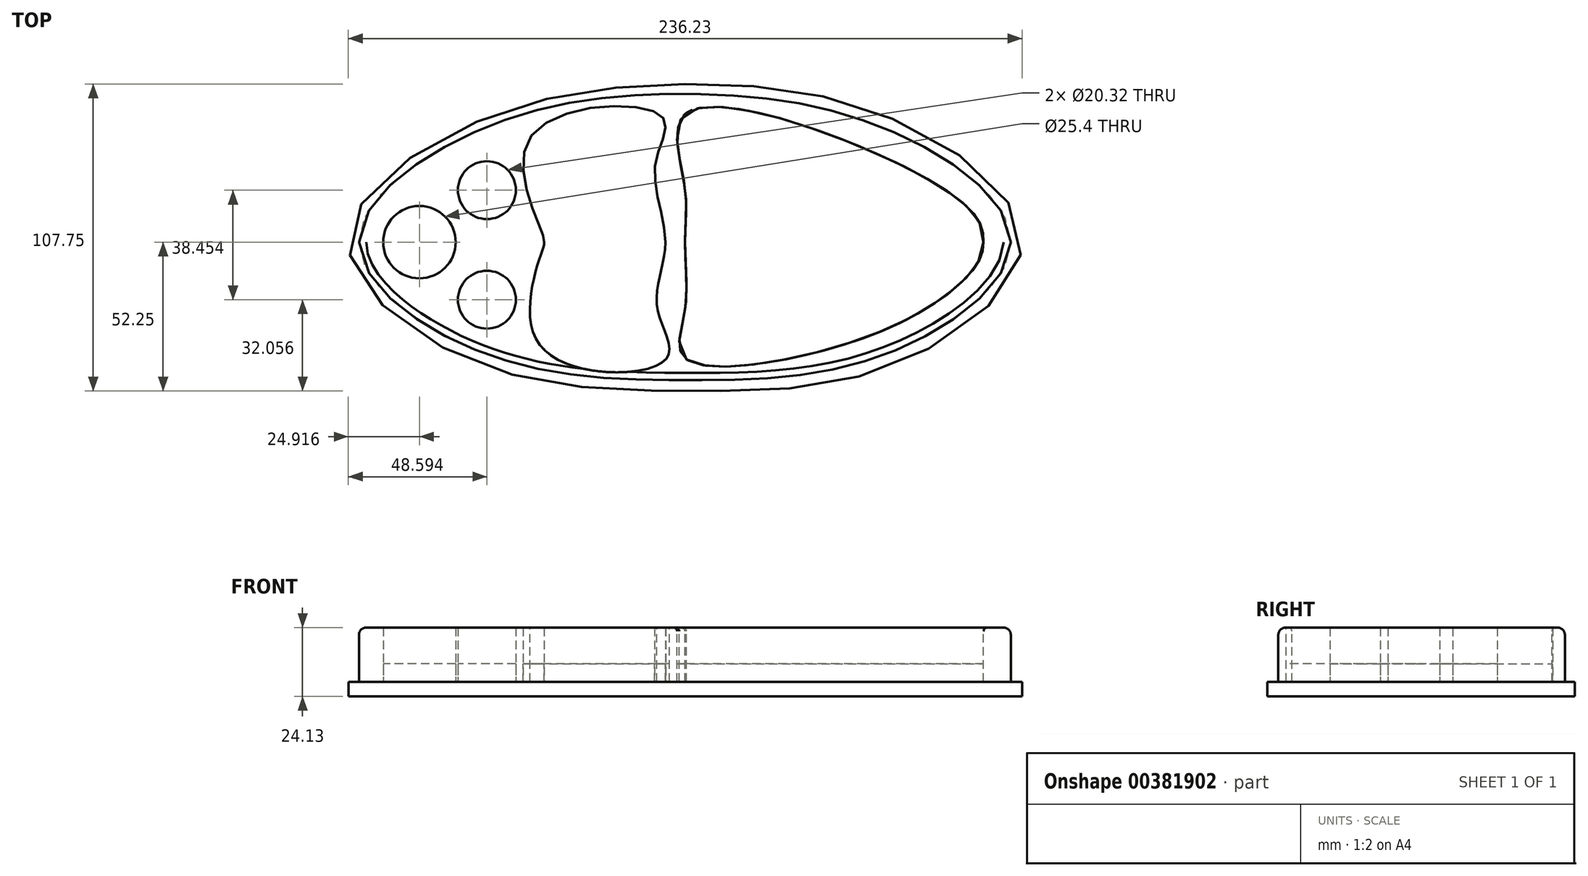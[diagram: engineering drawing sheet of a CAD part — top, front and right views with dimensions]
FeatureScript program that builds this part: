
annotation { "Feature Type Name" : "Feature", "Feature Type Description" : "" }
export const myFeature = defineFeature(function(context is Context, id is Id, definition is map)
    precondition{}
    {
        {
            var Q0;
            Q0=qCreatedBy(makeId("Top.planeOp"),FACE);
            var sketch = newSketch(context, id + "F0", { "sketchPlane" : qUnion([Q0])});
            skFitSpline(sketch, "E0", {"points": [v(0, 52.05) * mm, v(71.52, 39.35) * mm, v(114.3, 0) * mm, v(70.75, -39.18) * mm, v(0, -48.42) * mm, v(-70.9, -38.8) * mm, v(-114.3, 0) * mm, v(-71.29, 39.73) * mm, v(0, 52.05) * mm]});
            skLineSegment(sketch, "E1", {"start": v(0, 0) * mm, "end": v(114.3, 0) * mm});
            skLineSegment(sketch, "E2", {"start": v(0, 0) * mm, "end": v(-114.3, 0) * mm});
            skFitSpline(sketch, "E3", {"points": [v(0, 0) * mm, v(0, 19.22) * mm, v(0, 44.9) * mm, v(67.98, 30.72) * mm, v(102.72, 8.06) * mm, v(104.73, 0) * mm, v(102.22, -8.06) * mm, v(66.47, -32.23) * mm, v(0, -40.79) * mm, v(0, -24.17) * mm, v(0, 0) * mm]});
            skFitSpline(sketch, "E4", {"points": [v(-8.18, 44.25) * mm, v(-10.31, 27.87) * mm, v(-6.88, 0) * mm, v(-9.6, -23.4) * mm, v(-6.75, -41.2) * mm, v(-50.19, -36.93) * mm, v(-50.08, -3.13) * mm, v(-49.95, 2.91) * mm, v(-53.75, 37.49) * mm, v(-8.18, 44.25) * mm]});
            skCircle(sketch, "E5", {"center": v(-93.1, 0) * mm, "radius": 12.7 * mm});
            skCircle(sketch, "E6", {"center": v(-69.42, 18.26) * mm, "radius": 10.16 * mm});
            skCircle(sketch, "E7", {"center": v(-69.42, -20.2) * mm, "radius": 10.16 * mm});
            skSolve(sketch);
        }
        {
            var Q0;
            Q0=makeQuery(id+"F0.imprint","IMPRINT",FACE,{"disambiguationData":[TD([[makeQuery(id+"F0.imprint","IMPRINT",EDGE,{"derivedFrom":sQuery(id+"F0.wireOp",EDGE,"E6")}),1.0]])]});
            var Q1;
            {var subQ0=sQuery(id+"F0.wireOp",EDGE,"E5");var subQ1=sQuery(id+"F0.wireOp",EDGE,"E2");var subQ2=makeQuery(id+"F0.imprint","INTERSECT",VERTEX,{"disambiguationData":[OD(0.0)],"derivedFrom":[subQ1,subQ0]});Q1=makeQuery(id+"F0.imprint","IMPRINT",FACE,{"disambiguationData":[TD([[makeQuery(id+"F0.imprint","IMPRINT",EDGE,{"disambiguationData":[TD([[subQ2,-1.0]])],"derivedFrom":subQ1}),-1.0]])]});}
            var Q2;
            {var subQ0=sQuery(id+"F0.wireOp",EDGE,"E5");var subQ1=sQuery(id+"F0.wireOp",EDGE,"E2");var subQ2=makeQuery(id+"F0.imprint","INTERSECT",VERTEX,{"disambiguationData":[OD(0.0)],"derivedFrom":[subQ1,subQ0]});Q2=makeQuery(id+"F0.imprint","IMPRINT",FACE,{"disambiguationData":[TD([[makeQuery(id+"F0.imprint","IMPRINT",EDGE,{"disambiguationData":[TD([[subQ2,-1.0]])],"derivedFrom":subQ1}),1.0]])]});}
            var Q3;
            Q3=makeQuery(id+"F0.imprint","IMPRINT",FACE,{"disambiguationData":[TD([[makeQuery(id+"F0.imprint","IMPRINT",EDGE,{"derivedFrom":sQuery(id+"F0.wireOp",EDGE,"E7")}),1.0]])]});
            var Q4;
            {var subQ0=sQuery(id+"F0.wireOp",EDGE,"E4");var subQ1=sQuery(id+"F0.wireOp",EDGE,"E2");var subQ2=makeQuery(id+"F0.imprint","INTERSECT",VERTEX,{"disambiguationData":[OD(0.0)],"derivedFrom":[subQ1,subQ0]});Q4=makeQuery(id+"F0.imprint","IMPRINT",FACE,{"disambiguationData":[TD([[makeQuery(id+"F0.imprint","IMPRINT",EDGE,{"disambiguationData":[TD([[subQ2,-1.0]])],"derivedFrom":subQ1}),1.0]])]});}
            var Q5;
            {var subQ0=sQuery(id+"F0.wireOp",EDGE,"E4");var subQ1=sQuery(id+"F0.wireOp",EDGE,"E2");var subQ2=makeQuery(id+"F0.imprint","INTERSECT",VERTEX,{"disambiguationData":[OD(0.0)],"derivedFrom":[subQ1,subQ0]});Q5=makeQuery(id+"F0.imprint","IMPRINT",FACE,{"disambiguationData":[TD([[makeQuery(id+"F0.imprint","IMPRINT",EDGE,{"disambiguationData":[TD([[subQ2,-1.0]])],"derivedFrom":subQ1}),-1.0]])]});}
            var Q6;
            {var subQ0=sQuery(id+"F0.wireOp",EDGE,"E3");var subQ1=sQuery(id+"F0.wireOp",EDGE,"E1");var subQ3=makeQuery(id+"F0.imprint","INTERSECT",VERTEX,{"derivedFrom":[subQ1,subQ0]});Q6=makeQuery(id+"F0.imprint","IMPRINT",FACE,{"disambiguationData":[TD([[makeQuery(id+"F0.imprint","IMPRINT",EDGE,{"disambiguationData":[TD([[subQ3,1.0]])],"derivedFrom":subQ1}),1.0]])]});}
            var Q7;
            {var subQ0=sQuery(id+"F0.wireOp",EDGE,"E3");var subQ1=sQuery(id+"F0.wireOp",EDGE,"E1");var subQ3=makeQuery(id+"F0.imprint","INTERSECT",VERTEX,{"derivedFrom":[subQ1,subQ0]});Q7=makeQuery(id+"F0.imprint","IMPRINT",FACE,{"disambiguationData":[TD([[makeQuery(id+"F0.imprint","IMPRINT",EDGE,{"disambiguationData":[TD([[subQ3,1.0]])],"derivedFrom":subQ1}),-1.0]])]});}
            extrude(context, id + "F1", {"entities" : qUnion([Q0, Q1, Q2, Q3, Q4, Q5, Q6, Q7]), "depth" : 6.35 * mm});
        }
        {
            var Q0;
            Q0=makeQuery(id+"F0.imprint","IMPRINT",FACE,{"disambiguationData":[TD([[makeQuery(id+"F0.imprint","IMPRINT",EDGE,{"derivedFrom":sQuery(id+"F0.wireOp",EDGE,"E7")}),-1.0]])]});
            var Q1;
            Q1=makeQuery(id+"F0.imprint","IMPRINT",FACE,{"disambiguationData":[TD([[makeQuery(id+"F0.imprint","IMPRINT",EDGE,{"derivedFrom":sQuery(id+"F0.wireOp",EDGE,"E6")}),-1.0]])]});
            extrude(context, id + "F2", {"entities" : qUnion([Q0, Q1]), "depth" : 19.05 * mm});
        }
        {
            var Q0;
            Q0=qCreatedBy(makeId("Top.planeOp"),FACE);
            var sketch = newSketch(context, id + "F3", { "sketchPlane" : qUnion([Q0])});
            skFitSpline(sketch, "E8", {"points": [v(0, 55.48) * mm, v(72.62, 43.35) * mm, v(118.22, 0) * mm, v(72.62, -43.35) * mm, v(0, -52.16) * mm, v(-73, -42.38) * mm, v(-118, 0) * mm, v(-73.19, 42.17) * mm, v(0, 55.48) * mm]});
            skSolve(sketch);
        }
        {
            var Q0;
            Q0=makeQuery(id+"F3.imprint","IMPRINT",FACE,{"disambiguationData":[TD([[makeQuery(id+"F3.imprint","IMPRINT",EDGE,{"derivedFrom":sQuery(id+"F3.wireOp",EDGE,"E8")}),-1.0]])]});
            extrude(context, id + "F4", {"entities" : qUnion([Q0]), "oppositeDirection" : true, "depth" : 5.08 * mm});
        }
        {
            var Q0;
            Q0=makeQuery(id+"F2.opExtrude","CAP_EDGE",EDGE,{"disambiguationData":[OSD([sQuery(id+"F0.wireOp",EDGE,"E3")])],"isStart":false});
            fillet(context, id + "F5", {"entities" : qUnion([Q0]), "radius" : 1.27 * mm, "tangentPropagation" : true, "allowEdgeOverflow" : false});
        }
        {
            var Q0;
            Q0=makeQuery(id+"F2.opExtrude","CAP_EDGE",EDGE,{"disambiguationData":[OSD([sQuery(id+"F0.wireOp",EDGE,"E0")])],"isStart":false});
            fillet(context, id + "F6", {"entities" : qUnion([Q0]), "radius" : 2.54 * mm, "tangentPropagation" : true, "allowEdgeOverflow" : false});
        }
    });
